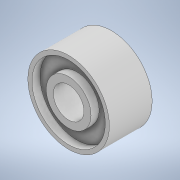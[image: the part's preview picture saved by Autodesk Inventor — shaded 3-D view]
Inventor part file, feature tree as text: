
AUTODESK INVENTOR PART (.ipt)
format: ipt  version: 2021 (Build 250183000, 183)  size: 133,120 bytes
history: native  units: in
note: dims shown in document units (in); Inventor stores cm internally (conversion verified against a paired STEP export)
features: extrude x3, sketch x3, plane x2
ambient origin geometry x8: Origin, YZ Plane, XZ Plane, XY Plane, X Axis, Y Axis, Z Axis, Center Point
bodies: Solid1 (feature_tree)
feature tree (8):
  extrude  "Extrusion1"  Depth=0.1732in
  plane  "Work Plane1"
  extrude  "Extrusion2"  Depth=0.1654in TaperAngle=0.0deg
  plane  "Work Plane2"
  extrude  "Extrusion3"  Depth=0.0315in
  sketch  "Sketch1"  dims[d0=0.1181in d1=0.1732in]
  sketch  "Sketch2"  dims[d2=0.315in d3=0.1654in d4=0.0in]
  sketch  "Sketch3"  dims[d5=0.0in d6=0.1732in d7=0.2835in d8=0.0315in d9=0.0in d10=0.0in d11=0.0315in d12=0.0in]
